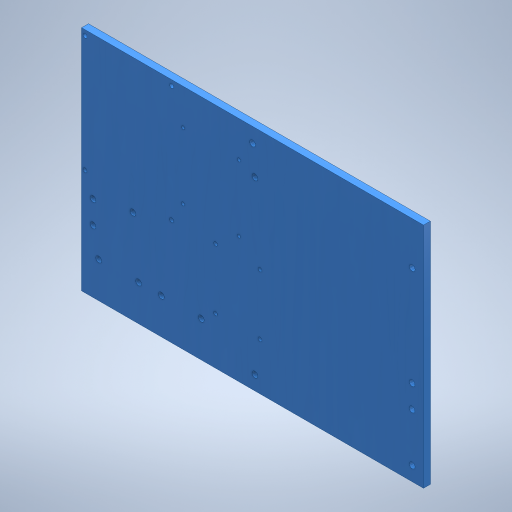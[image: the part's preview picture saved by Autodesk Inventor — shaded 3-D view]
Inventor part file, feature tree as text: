
AUTODESK INVENTOR PART (.ipt)
format: ipt  version: 2023 (Build 270158000, 158)  size: 276,992 bytes
history: native  units: mm
features: reference x26, other x13, extrude x2, sketch x2
ambient origin geometry x8: Origin, YZ Plane, XZ Plane, XY Plane, X Axis, Y Axis, Z Axis, Center Point
bodies: Solid1 (feature_tree)
feature tree (43):
  extrude  "Extrusion1"  Depth=200.0mm
  extrude  "Extrusion2"  Depth=300.0mm TaperAngle=0.0deg
  sketch  "Sketch1"  dims[d0=6.0mm d1=0.0mm d2=200.0mm]
  sketch  "Sketch2"  dims[d3=300.0mm d4=30.0mm d5=0.0mm]
  reference  "Reference1"
  reference  "Reference2"
  reference  "Reference3"
  reference  "Reference4"
  reference  "Reference5"
  reference  "Reference6"
  reference  "Reference7"
  reference  "Reference8"
  reference  "Reference9"
  reference  "Reference10"
  reference  "Reference11"
  reference  "Reference12"
  reference  "Reference13"
  reference  "Reference14"
  reference  "Reference15"
  reference  "Reference16"
  reference  "Reference17"
  reference  "Reference18"
  reference  "Reference19"
  reference  "Reference20"
  reference  "Reference21"
  reference  "Reference22"
  reference  "Reference23"
  reference  "Reference24"
  reference  "Reference25"
  reference  "Reference26"
  other  "<userpath>\OneDrive\ClawdDrive\Objet3D\3DPrinter\inventor\3DPrinterBeltCoreXY.iam"
  other  "3DPrinterBeltCoreXY.iam"
  other  "PSUBracketPowerConnector:1"
  other  "PSUBracket:1"
  other  "RelayBracket:2"
  other  "RelayBracket:1"
  other  "dc-dc SZBK07:1"
  other  "Raspberry Pi 4 Model B:1"
  other  "mks sgen l v2.0:1"
  other  "BracketControlPannel:1"
  other  "BracketControlPannel:2"
  other  "FanSpace:1"
  other  "FanSpace:2"
